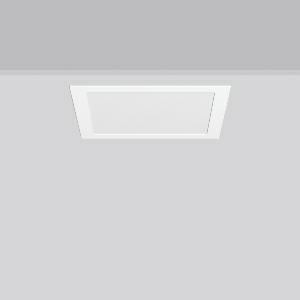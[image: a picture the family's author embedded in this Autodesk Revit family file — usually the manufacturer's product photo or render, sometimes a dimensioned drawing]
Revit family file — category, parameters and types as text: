
# Revit family: toledo_flat_square_e_901671_002_730_c40b
name_source: partatom
category: Lighting Fixtures
units: mm (PartAtom-declared; Revit-internal decimal feet)

## family parameters
Cut with Voids When Loaded = No
Host = Face
Light Source = No
Part Type = Normal
Room Calculation Point = No
Round Connector Dimension = Use Diameter
Shared = No

## types (1)
- TuneableWhite 846 (1 x LED Modul 846, 2400 lm, 4600)
    Apparent Load = 24 VA
    CIE Flux Codes = 47 79 96 100 100
    Color Rendering = 80
    Color Temperature = 4600
    Default Elevation = 1800 mm
    Description = Series: TOLEDO FLAT square
Ultra thin recessed downlight. Housing: die-cast aluminium. Light guide and diffuser made of non-yellowing PMMA, opal matt. Tunable white dynamically adjustable from 2700 K to 6500 K.With Casambi smart+free Bluetooth control for wireless network and operation using Android / iOS devices, free app available for download. Ceiling installation with spring system. Mounting depth depends on ceiling strength. Surface mounted housing as accessory for all sizes. Retrofittable decorative cylinders made of chintz fabric as accessory, optional with satin finish plastic diffuser. Through-wiring box (5 pole) available as accessory. 
Colour: white
Length: 300 mm
Width: 300 mm
Height: 3 mm
Cut-out length: 280 mm
Cut-out width: 280 mm
Recess height: 55-75 mm
Luminaire: recess height: 31-51 mm
Lamp: LED
Socket: without socket
Colour temperature: 2700K - 6500K
Colour rendering index (CRI): 80
System power: 24 W
Rated luminous flux: 2400 lm
Luminous efficiency: 100 lm/W
System power 2: 26 W
Rated luminous flux 2: 2200 lm
Luminous efficiency 2: 85 lm/W
System power 3: 24 W
Rated luminous flux 3: 2300 lm
Luminous efficiency 3: 96 lm/W
Control gear: Dimmable Bluetooth converter
Protection class: II
Type of protection: IP 54
    Height = 0 mm  [stored 0 ft]
    Lamp = 1 x LED Modul 846
    Lamp Light Flux = 2400 lm
    Lamp count = 1
    Length = 300 mm
    Lifetime = 50000 h
    Luminous efficacy = 100 lm/W
    Manufacturer = RZB
    ModVariant = No
    Model = 901671.002.730
    Mounting Place = Ceiling
    Mounting Type = Recessed
    Number of Poles = 1
    OnlyDefault = Yes
    Power Factor = 1
    Product Name = TOLEDO FLAT square E
    Product group = Recessed downlights
    ProductGroupID = 402
    Protection Class = Protection class II
    Protection Degree = IP 20
    RLX_Detail_Level = 1
    RLX_Emergency_Light_Flux = 0 lm
    RLX_Emergency_Type = 0
    RLX_Emergency_Type_DB = No
    RlxData = <blob elided: 60629 chars, md5=f20d37da>
    Socket = socket
    Standby Power = 0 W
    System Light Flux = 2400 lm
    System Power = 24 W
    Type Comments = TuneableWhite 846
    Type Image = 901488.002.jpg
    URL = http://relux.com
    VarID = tuneablewhite_846
    Voltage = 230 V
    Voltage Range = 220-240 V
    Weight = 0.00 kg
    Width = 300 mm

note: [stored X ft] marks values corroborated as IEEE doubles in the binary element streams (Revit-internal decimal feet)

## geometry (parser evidence)
native form markers: Blend x4, Sweep x12
no freeform markers — native parametric forms only
